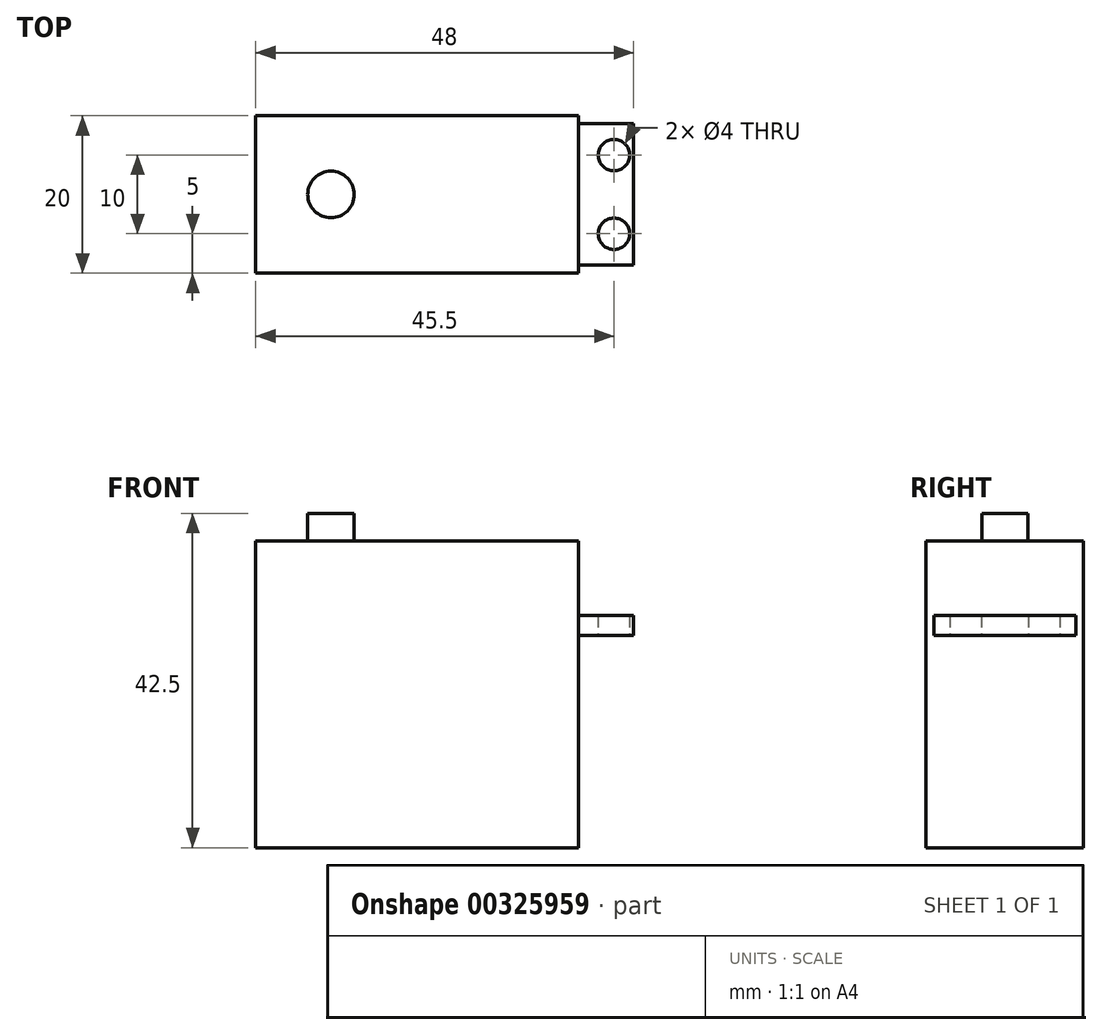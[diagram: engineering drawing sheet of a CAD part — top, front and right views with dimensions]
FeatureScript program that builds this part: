
annotation { "Feature Type Name" : "Feature", "Feature Type Description" : "" }
export const myFeature = defineFeature(function(context is Context, id is Id, definition is map)
    precondition{}
    {
        {
            var Q0;
            Q0=qCreatedBy(makeId("Top.planeOp"),FACE);
            var sketch = newSketch(context, id + "F0", { "sketchPlane" : qUnion([Q0])});
            skLineSegment(sketch, "E0.bottom", {"start": v(20.5, 10) * mm, "end": v(-20.5, 10) * mm});
            skLineSegment(sketch, "E0.top", {"start": v(20.5, -10) * mm, "end": v(-20.5, -10) * mm});
            skLineSegment(sketch, "E0.left", {"start": v(20.5, 10) * mm, "end": v(20.5, -10) * mm});
            skLineSegment(sketch, "E0.right", {"start": v(-20.5, 10) * mm, "end": v(-20.5, -10) * mm});
            skPoint(sketch, "E0.middle", {"position": v(0, 0) * mm});
            skSolve(sketch);
        }
        {
            var Q0;
            Q0=makeQuery(id+"F0.imprint","IMPRINT",FACE,{"disambiguationData":[TD([[makeQuery(id+"F0.imprint","IMPRINT",EDGE,{"derivedFrom":sQuery(id+"F0.wireOp",EDGE,"E0.bottom")}),1.0]])]});
            extrude(context, id + "F1", {"entities" : qUnion([Q0]), "depth" : 27 * mm});
        }
        {
            var Q0;
            Q0=makeQuery(id+"F1.opExtrude","CAP_FACE",FACE,{"disambiguationData":[OSD([sQuery(id+"F0.wireOp",EDGE,"E0.bottom"),sQuery(id+"F0.wireOp",EDGE,"E0.top"),sQuery(id+"F0.wireOp",EDGE,"E0.left"),sQuery(id+"F0.wireOp",EDGE,"E0.right")])],"isStart":false});
            var sketch = newSketch(context, id + "F2", { "sketchPlane" : qUnion([Q0])});
            skLineSegment(sketch, "E1.0", {"start": v(20.5, 10) * mm, "end": v(-20.5, 10) * mm});
            skLineSegment(sketch, "E2.0", {"start": v(-20.5, 10) * mm, "end": v(-20.5, -10) * mm});
            skLineSegment(sketch, "E3.0", {"start": v(20.5, -10) * mm, "end": v(-20.5, -10) * mm});
            skLineSegment(sketch, "E4.bottom", {"start": v(27.5, 9) * mm, "end": v(20.5, 9) * mm});
            skLineSegment(sketch, "E4.top", {"start": v(27.5, -9) * mm, "end": v(20.5, -9) * mm});
            skLineSegment(sketch, "E4.left", {"start": v(27.5, 9) * mm, "end": v(27.5, -9) * mm});
            skLineSegment(sketch, "E4.right", {"start": v(20.5, 9) * mm, "end": v(20.5, -9) * mm});
            skPoint(sketch, "E4.middle", {"position": v(24, 0) * mm});
            skPoint(sketch, "E4.middle.positionSnap0", {"position": v(20.5, 0) * mm});
            skPoint(sketch, "E4.centerSnap0", {"position": v(20.5, 0) * mm});
            skCircle(sketch, "E5", {"center": v(25, 5) * mm, "radius": 2 * mm});
            skCircle(sketch, "E6.MirrorC", {"center": v(25, -5) * mm, "radius": 2 * mm});
            skLineSegment(sketch, "E7.MirrorCS", {"start": v(-20.5, 9) * mm, "end": v(-20.5, -9) * mm});
            skLineSegment(sketch, "E8.MirrorCS", {"start": v(-27.5, 9) * mm, "end": v(-20.5, 9) * mm});
            skLineSegment(sketch, "E9.MirrorCS", {"start": v(-27.5, 9) * mm, "end": v(-27.5, -9) * mm});
            skLineSegment(sketch, "E10.MirrorCS", {"start": v(-27.5, -9) * mm, "end": v(-20.5, -9) * mm});
            skCircle(sketch, "E11.MirrorC", {"center": v(-25, -5) * mm, "radius": 2 * mm});
            skCircle(sketch, "E12.MirrorC", {"center": v(-25, 5) * mm, "radius": 2 * mm});
            skSolve(sketch);
        }
        {
            var Q0;
            {var subQ3=sQuery(id+"F2.wireOp",EDGE,"E1.0");Q0=makeQuery(id+"F2.imprint","IMPRINT",FACE,{"disambiguationData":[TD([[makeQuery(id+"F2.imprint","IMPRINT",EDGE,{"derivedFrom":subQ3}),1.0]])]});}
            var Q1;
            Q1=makeQuery(id+"F2.imprint","IMPRINT",FACE,{"disambiguationData":[TD([[makeQuery(id+"F2.imprint","IMPRINT",EDGE,{"derivedFrom":sQuery(id+"F2.wireOp",EDGE,"E4.bottom")}),1.0]])]});
            var Q2;
            Q2=makeQuery(id+"F2.imprint","IMPRINT",FACE,{"disambiguationData":[TD([[makeQuery(id+"F2.imprint","IMPRINT",EDGE,{"derivedFrom":sQuery(id+"F2.wireOp",EDGE,"E7.MirrorCS")}),-1.0]])]});
            extrude(context, id + "F3", {"entities" : qUnion([Q0, Q1, Q2]), "operationType" : NewBodyOperationType.ADD, "depth" : 2.5 * mm});
        }
        {
            var Q0;
            {var subQ3=sQuery(id+"F2.wireOp",EDGE,"E1.0");Q0=makeQuery(id+"F2.imprint","IMPRINT",FACE,{"disambiguationData":[TD([[makeQuery(id+"F2.imprint","IMPRINT",EDGE,{"derivedFrom":subQ3}),1.0]])]});}
            extrude(context, id + "F4", {"entities" : qUnion([Q0]), "operationType" : NewBodyOperationType.ADD, "depth" : 12 * mm});
        }
        {
            var Q0;
            Q0=makeQuery(id+"F4.opExtrude","CAP_FACE",FACE,{"disambiguationData":[OSD([sQuery(id+"F0.wireOp",EDGE,"E0.left"),sQuery(id+"F2.wireOp",EDGE,"E1.0"),sQuery(id+"F2.wireOp",EDGE,"E2.0"),sQuery(id+"F2.wireOp",EDGE,"E3.0"),sQuery(id+"F2.wireOp",EDGE,"E4.right"),sQuery(id+"F2.wireOp",EDGE,"E7.MirrorCS")])],"isStart":false});
            var sketch = newSketch(context, id + "F5", { "sketchPlane" : qUnion([Q0])});
            skCircle(sketch, "E13", {"center": v(-10.95, 0) * mm, "radius": 2.95 * mm});
            skPoint(sketch, "E13.centerSnap0", {"position": v(-20.5, 0) * mm});
            skSolve(sketch);
        }
        {
            var Q0;
            Q0=makeQuery(id+"F5.imprint","IMPRINT",FACE,{"disambiguationData":[TD([[makeQuery(id+"F5.imprint","IMPRINT",EDGE,{"derivedFrom":sQuery(id+"F5.wireOp",EDGE,"E13")}),1.0]])]});
            extrude(context, id + "F6", {"entities" : qUnion([Q0]), "operationType" : NewBodyOperationType.ADD, "depth" : 3.5 * mm});
        }
    });
